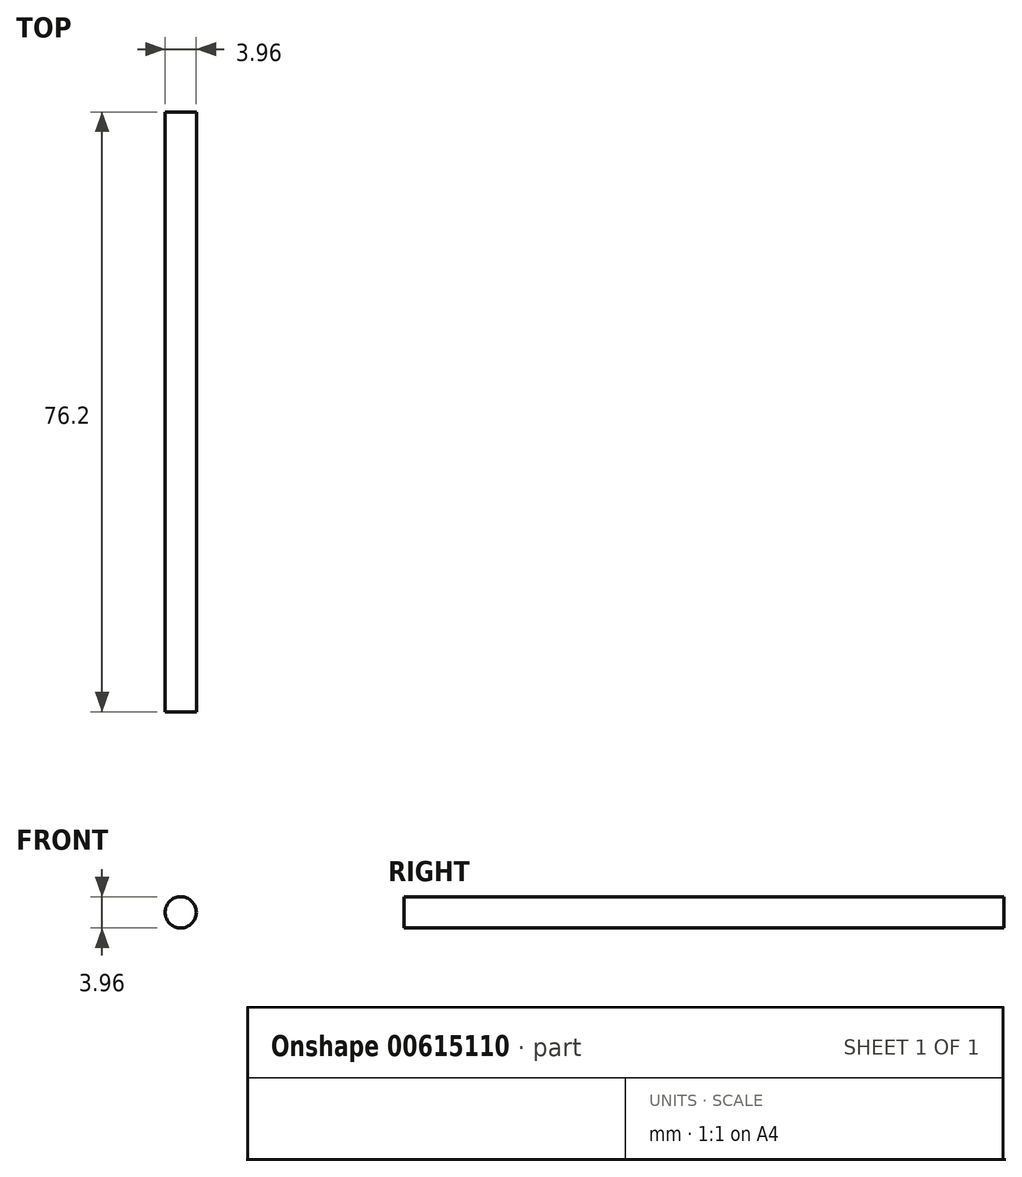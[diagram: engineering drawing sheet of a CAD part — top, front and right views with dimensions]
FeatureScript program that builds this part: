
annotation { "Feature Type Name" : "Feature", "Feature Type Description" : "" }
export const myFeature = defineFeature(function(context is Context, id is Id, definition is map)
    precondition{}
    {
        {
            var Q0;
            Q0=qCreatedBy(makeId("Front.planeOp"),FACE);
            var sketch = newSketch(context, id + "F0", { "sketchPlane" : qUnion([Q0])});
            skCircle(sketch, "E0", {"center": v(0, 0) * mm, "radius": 1.98 * mm});
            skSolve(sketch);
        }
        {
            var Q0;
            Q0 = qSketchRegion(id + "F0", true);
            extrude(context, id + "F1", {"entities" : qUnion([Q0]), "endBound" : BoundingType.SYMMETRIC, "depth" : 76.2 * mm, "offsetDistance" : 25.4 * mm});
        }
    });
